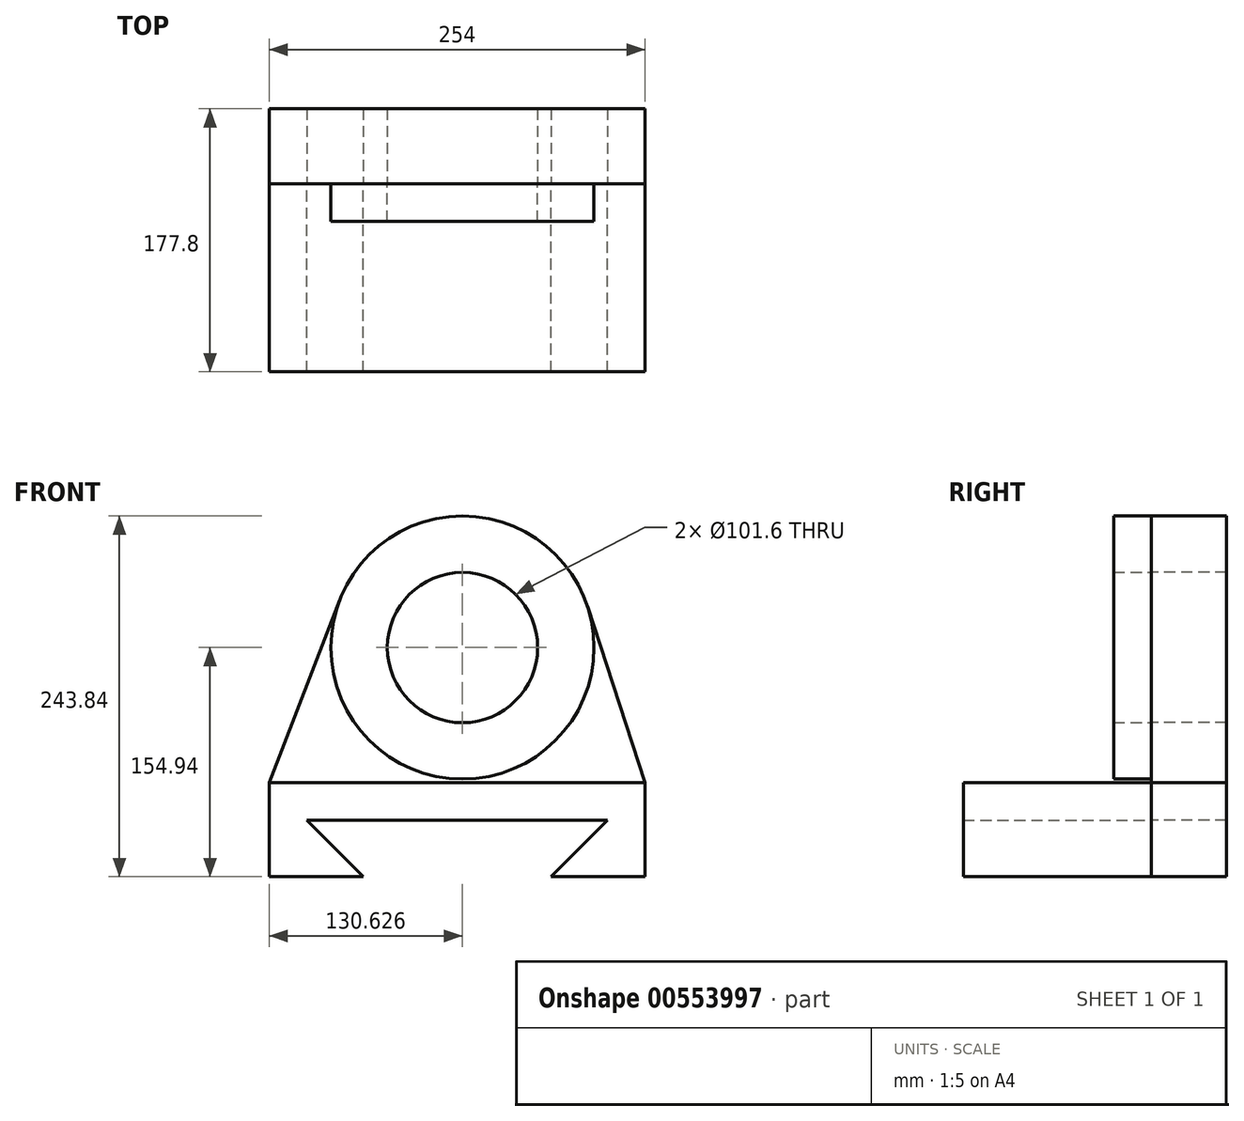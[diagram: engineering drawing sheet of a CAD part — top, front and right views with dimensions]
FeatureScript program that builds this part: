
annotation { "Feature Type Name" : "Feature", "Feature Type Description" : "" }
export const myFeature = defineFeature(function(context is Context, id is Id, definition is map)
    precondition{}
    {
        {
            var Q0;
            Q0=qCreatedBy(makeId("Front.planeOp"),FACE);
            var sketch = newSketch(context, id + "F0", { "sketchPlane" : qUnion([Q0])});
            skLineSegment(sketch, "E0", {"start": v(0, 0) * mm, "end": v(254, 0) * mm});
            skLineSegment(sketch, "E1", {"start": v(0, 0) * mm, "end": v(0, -63.5) * mm});
            skLineSegment(sketch, "E2", {"start": v(0, -63.5) * mm, "end": v(63.5, -63.5) * mm});
            skLineSegment(sketch, "E3", {"start": v(254, 0) * mm, "end": v(254, -63.5) * mm});
            skLineSegment(sketch, "E4", {"start": v(254, -63.5) * mm, "end": v(190.5, -63.5) * mm});
            skLineSegment(sketch, "E5", {"start": v(63.5, -63.5) * mm, "end": v(25.4, -25.4) * mm});
            skLineSegment(sketch, "E6", {"start": v(25.4, -25.4) * mm, "end": v(63.5, -25.4) * mm});
            skLineSegment(sketch, "E7", {"start": v(63.5, -25.4) * mm, "end": v(190.5, -25.4) * mm});
            skLineSegment(sketch, "E8", {"start": v(190.5, -25.4) * mm, "end": v(228.6, -25.4) * mm});
            skLineSegment(sketch, "E9", {"start": v(190.5, -63.5) * mm, "end": v(228.6, -25.4) * mm});
            skCircle(sketch, "E10", {"center": v(130.63, 91.44) * mm, "radius": 88.9 * mm});
            skCircle(sketch, "E11", {"center": v(130.63, 91.44) * mm, "radius": 50.8 * mm});
            skLineSegment(sketch, "E12", {"start": v(0, 0) * mm, "end": v(47.7, 123.47) * mm});
            skLineSegment(sketch, "E13", {"start": v(254, 0) * mm, "end": v(215.14, 119.03) * mm});
            skSolve(sketch);
        }
        {
            var Q0;
            Q0=makeQuery(id+"F0.imprint","IMPRINT",FACE,{"disambiguationData":[TD([[makeQuery(id+"F0.imprint","IMPRINT",EDGE,{"derivedFrom":sQuery(id+"F0.wireOp",EDGE,"E0")}),-1.0]])]});
            extrude(context, id + "F1", {"entities" : qUnion([Q0]), "depth" : 127 * mm, "offsetDistance" : 25.4 * mm});
        }
        {
            var Q0;
            Q0=makeQuery(id+"F0.imprint","IMPRINT",FACE,{"disambiguationData":[TD([[makeQuery(id+"F0.imprint","IMPRINT",EDGE,{"derivedFrom":sQuery(id+"F0.wireOp",EDGE,"E11")}),-1.0]])]});
            extrude(context, id + "F2", {"entities" : qUnion([Q0]), "depth" : 25.4 * mm, "offsetDistance" : 25.4 * mm});
        }
        {
            var Q0;
            Q0=makeQuery(id+"F0.imprint","IMPRINT",FACE,{"disambiguationData":[TD([[makeQuery(id+"F0.imprint","IMPRINT",EDGE,{"derivedFrom":sQuery(id+"F0.wireOp",EDGE,"E11")}),-1.0]])]});
            var Q1;
            Q1=makeQuery(id+"F0.imprint","IMPRINT",FACE,{"disambiguationData":[TD([[makeQuery(id+"F0.imprint","IMPRINT",EDGE,{"derivedFrom":sQuery(id+"F0.wireOp",EDGE,"E0")}),1.0]])]});
            var Q2;
            Q2=makeQuery(id+"F0.imprint","IMPRINT",FACE,{"disambiguationData":[TD([[makeQuery(id+"F0.imprint","IMPRINT",EDGE,{"derivedFrom":sQuery(id+"F0.wireOp",EDGE,"E0")}),-1.0]])]});
            extrude(context, id + "F3", {"entities" : qUnion([Q0, Q1, Q2]), "oppositeDirection" : true, "depth" : 50.8 * mm, "offsetDistance" : 25.4 * mm});
        }
    });
